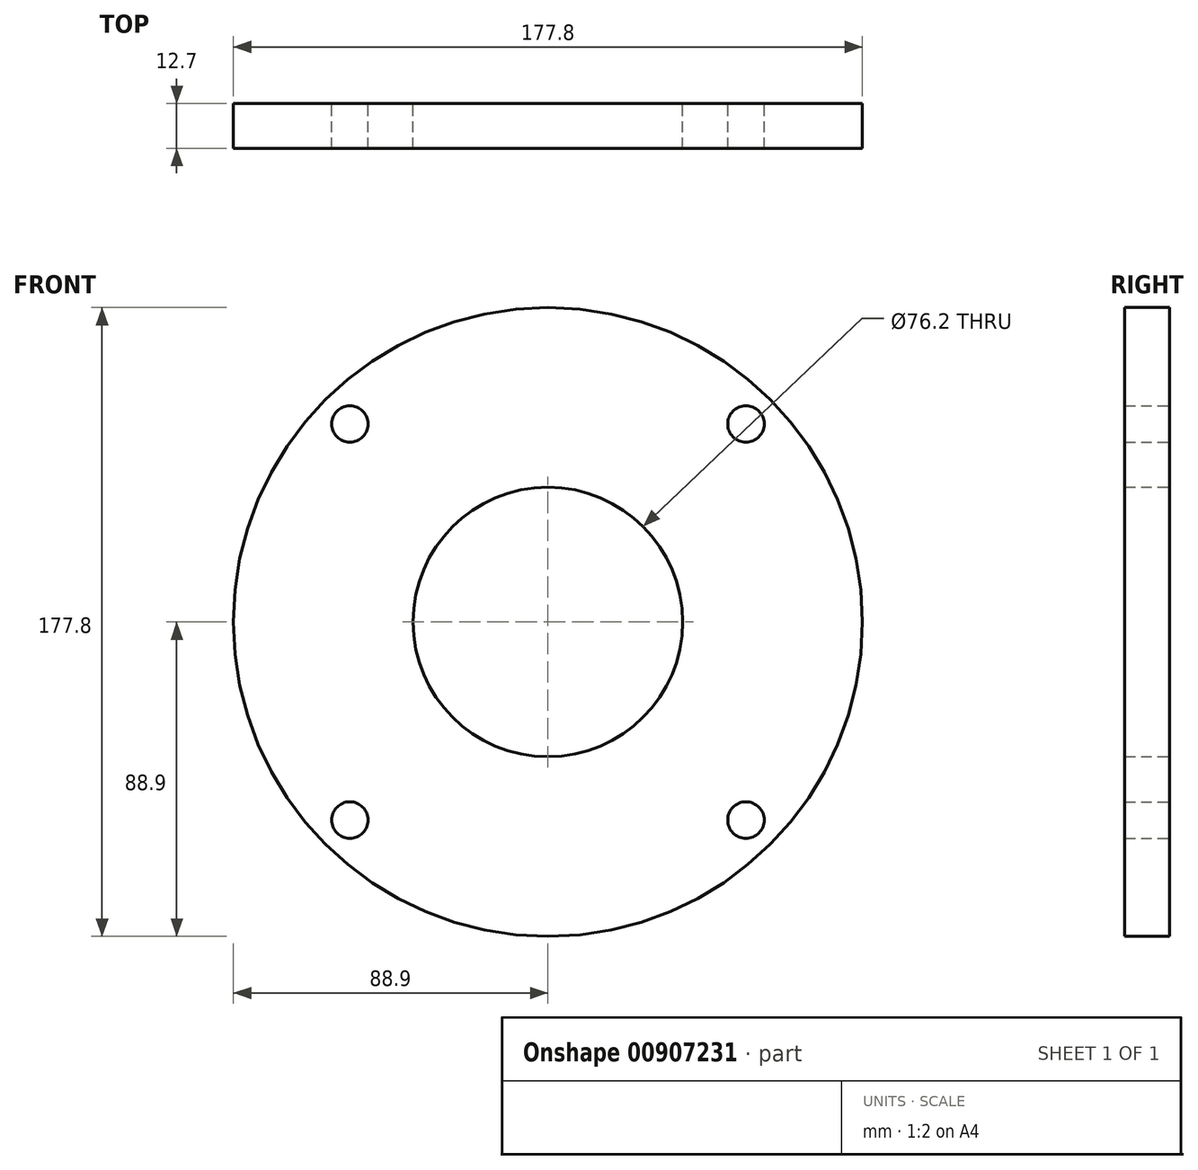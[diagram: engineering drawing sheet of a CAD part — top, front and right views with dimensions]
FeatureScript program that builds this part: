
annotation { "Feature Type Name" : "Feature", "Feature Type Description" : "" }
export const myFeature = defineFeature(function(context is Context, id is Id, definition is map)
    precondition{}
    {
        {
            var Q0;
            Q0=qCreatedBy(makeId("Front.planeOp"),FACE);
            var sketch = newSketch(context, id + "F0", { "sketchPlane" : qUnion([Q0])});
            skCircle(sketch, "E0", {"center": v(0, 0) * mm, "radius": 88.9 * mm});
            skCircle(sketch, "E1", {"center": v(0, 0) * mm, "radius": 38.1 * mm});
            skSolve(sketch);
        }
        {
            var Q0;
            Q0 = qSketchRegion(id + "F0", true);
            extrude(context, id + "F1", {"entities" : qUnion([Q0]), "depth" : 12.7 * mm, "offsetDistance" : 25.4 * mm});
        }
        {
            var Q0;
            Q0=makeQuery(id+"F1.opExtrude","CAP_FACE",FACE,{"disambiguationData":[OSD([sQuery(id+"F0.wireOp",EDGE,"E0"),sQuery(id+"F0.wireOp",EDGE,"E1")])],"isStart":false});
            var sketch = newSketch(context, id + "F2", { "sketchPlane" : qUnion([Q0])});
            skLineSegment(sketch, "E2", {"start": v(0, 0) * mm, "end": v(-62.86, 62.86) * mm, "construction": true});
            skPoint(sketch, "E3.center", {"position": v(0, 0) * mm});
            skLineSegment(sketch, "E4", {"start": v(0, 0) * mm, "end": v(62.86, 62.86) * mm, "construction": true});
            skLineSegment(sketch, "E5", {"start": v(0, 0) * mm, "end": v(-62.86, -62.86) * mm, "construction": true});
            skLineSegment(sketch, "E6", {"start": v(0, 0) * mm, "end": v(62.86, -62.86) * mm, "construction": true});
            skPoint(sketch, "E7", {"position": v(-62.86, 62.86) * mm});
            skPoint(sketch, "E8", {"position": v(62.86, 62.86) * mm});
            skPoint(sketch, "E9", {"position": v(62.86, -62.86) * mm});
            skPoint(sketch, "E10", {"position": v(-62.86, -62.86) * mm});
            skCircle(sketch, "E11", {"center": v(-56, 56) * mm, "radius": 7 * mm});
            skCircle(sketch, "E12", {"center": v(56, 56) * mm, "radius": 7 * mm});
            skCircle(sketch, "E13", {"center": v(56, -56) * mm, "radius": 7 * mm});
            skCircle(sketch, "E14", {"center": v(-56, -56) * mm, "radius": 7 * mm});
            skSolve(sketch);
        }
        {
            var Q0;
            Q0=sQuery(id+"F2.wireOp",VERTEX,"E11.center");
            var Q1;
            Q1=sQuery(id+"F2.wireOp",VERTEX,"E12.center");
            var Q2;
            Q2=sQuery(id+"F2.wireOp",VERTEX,"E13.center");
            var Q3;
            Q3=sQuery(id+"F2.wireOp",VERTEX,"E14.center");
            var Q4;
            Q4=makeQuery(id+"F1.opExtrude","SWEPT_BODY",BODY,{"disambiguationData":[OSD([sQuery(id+"F0.wireOp",EDGE,"E0"),sQuery(id+"F0.wireOp",EDGE,"E1")])]});
            hole(context, id + "F3", {"style" : HoleStyle.SIMPLE, "endStyle" : HoleEndStyle.THROUGH, "standardTappedOrClearance" : lookupTablePath({ "fit" : "Normal (ASME)", "standard" : "ANSI", "size" : "3/8", "type" : "Clearance" }), "standardBlindInLast" : lookupTablePath({ "fit" : "Normal", "standard" : "ANSI", "engagement" : "75%", "pitch" : "16 tpi", "size" : "3/8", "type" : "Clearance & tapped" }), "holeDiameter" : 10.3 * mm, "majorDiameter" : 9.52 * mm, "isTappedThrough" : true, "tappedDepth" : 8.47 * mm, "tapClearance" : 3, "locations" : qUnion([Q0, Q1, Q2, Q3]), "scope" : qUnion([Q4]), "startStyle" : HoleStartStyle.SKETCH});
        }
    });
